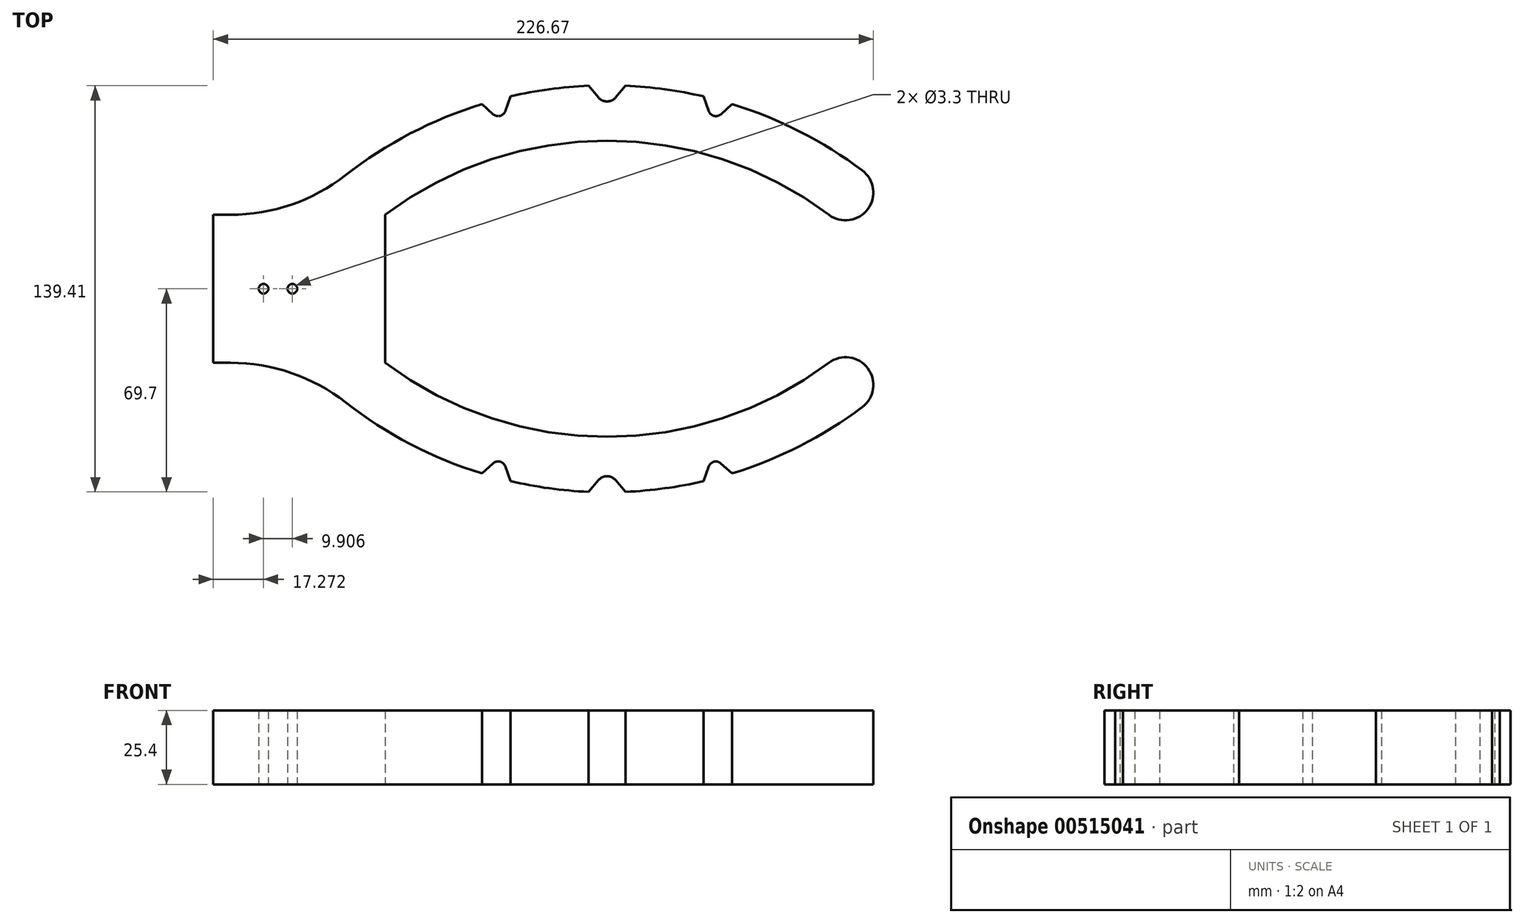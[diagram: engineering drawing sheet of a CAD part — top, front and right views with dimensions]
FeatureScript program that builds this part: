
annotation { "Feature Type Name" : "Feature", "Feature Type Description" : "" }
export const myFeature = defineFeature(function(context is Context, id is Id, definition is map)
    precondition{}
    {
        {
            var Q0;
            Q0=qCreatedBy(makeId("Top.planeOp"),FACE);
            var sketch = newSketch(context, id + "F0", { "sketchPlane" : qUnion([Q0])});
            skLineSegment(sketch, "E0.bottom", {"start": v(0, 0) * mm, "end": v(5.97, 0) * mm});
            skLineSegment(sketch, "E0.top", {"start": v(0, -50.8) * mm, "end": v(5.97, -50.8) * mm});
            skLineSegment(sketch, "E0.left", {"start": v(0, 0) * mm, "end": v(0, -50.8) * mm});
            skArc(sketch, "E1", {"start": v(211.43, 0) * mm, "mid": v(135.23, 25.4) * mm, "end": v(59.03, 0) * mm});
            skArc(sketch, "E2", {"start": v(59.06, -50.8) * mm, "mid": v(135.24, -76.19) * mm, "end": v(211.43, -50.8) * mm});
            skArc(sketch, "E3.0", {"start": v(222.86, 15.24) * mm, "mid": v(133.84, 44.44) * mm, "end": v(45.4, 13.56) * mm});
            skArc(sketch, "E4.0", {"start": v(45.45, -64.37) * mm, "mid": v(133.87, -95.23) * mm, "end": v(222.85, -66.04) * mm});
            skArc(sketch, "E5", {"start": v(211.43, 0) * mm, "mid": v(224.76, 1.9) * mm, "end": v(222.86, 15.24) * mm});
            skArc(sketch, "E6", {"start": v(222.85, -66.04) * mm, "mid": v(224.76, -52.7) * mm, "end": v(211.43, -50.8) * mm});
            skArc(sketch, "E7", {"start": v(5.97, 0) * mm, "mid": v(26.82, 3.48) * mm, "end": v(45.4, 13.56) * mm});
            skArc(sketch, "E8", {"start": v(45.45, -64.37) * mm, "mid": v(26.84, -54.29) * mm, "end": v(5.97, -50.8) * mm});
            skLineSegment(sketch, "E9", {"start": v(59.03, 0) * mm, "end": v(59.06, -50.8) * mm});
            skLineSegment(sketch, "E10", {"start": v(135.24, 50.81) * mm, "end": v(135.23, -101.6) * mm});
            skLineSegment(sketch, "E11", {"start": v(132.32, -91.04) * mm, "end": v(128.88, -95.1) * mm});
            skLineSegment(sketch, "E12", {"start": v(138.13, -91.04) * mm, "end": v(141.58, -95.1) * mm});
            skPoint(sketch, "E13.visualSharp", {"position": v(135.23, -87.62) * mm});
            skArc(sketch, "E13.filletArc", {"start": v(138.13, -91.04) * mm, "mid": v(135.23, -89.7) * mm, "end": v(132.32, -91.04) * mm});
            skLineSegment(sketch, "E14", {"start": v(135.23, -25.4) * mm, "end": v(230, -25.4) * mm});
            skLineSegment(sketch, "E15.MirrorCS", {"start": v(138.15, 40.25) * mm, "end": v(141.6, 44.31) * mm});
            skArc(sketch, "E16.MirrorCS", {"start": v(138.15, 40.25) * mm, "mid": v(135.24, 38.9) * mm, "end": v(132.34, 40.25) * mm});
            skLineSegment(sketch, "E17.MirrorCS", {"start": v(132.34, 40.25) * mm, "end": v(128.9, 44.31) * mm});
            skLineSegment(sketch, "E18", {"start": v(97.14, 50.81) * mm, "end": v(97.14, -102.44) * mm});
            skLineSegment(sketch, "E19", {"start": v(173.34, 50.81) * mm, "end": v(173.34, -98.72) * mm});
            skLineSegment(sketch, "E20", {"start": v(97.14, 39.4) * mm, "end": v(101.8, 20.92) * mm});
            skLineSegment(sketch, "E21", {"start": v(92.26, 37.99) * mm, "end": v(96.19, 34.5) * mm});
            skLineSegment(sketch, "E22", {"start": v(100.27, 35.56) * mm, "end": v(102.07, 40.64) * mm});
            skPoint(sketch, "E23.visualSharp", {"position": v(99, 32) * mm});
            skArc(sketch, "E23.filletArc", {"start": v(96.19, 34.5) * mm, "mid": v(98.5, 33.95) * mm, "end": v(100.27, 35.56) * mm});
            skLineSegment(sketch, "E24.MirrorCS", {"start": v(170.21, 35.55) * mm, "end": v(168.41, 40.63) * mm});
            skArc(sketch, "E25.MirrorCS", {"start": v(174.3, 34.5) * mm, "mid": v(171.97, 33.94) * mm, "end": v(170.21, 35.55) * mm});
            skLineSegment(sketch, "E26.MirrorCS", {"start": v(178.22, 37.98) * mm, "end": v(174.3, 34.5) * mm});
            skLineSegment(sketch, "E27.MirrorCS", {"start": v(178.2, -88.77) * mm, "end": v(174.28, -85.3) * mm});
            skArc(sketch, "E28.MirrorCS", {"start": v(174.28, -85.3) * mm, "mid": v(171.96, -84.74) * mm, "end": v(170.2, -86.35) * mm});
            skLineSegment(sketch, "E29.MirrorCS", {"start": v(170.2, -86.35) * mm, "end": v(168.4, -91.42) * mm});
            skLineSegment(sketch, "E30.MirrorCS", {"start": v(92.25, -88.76) * mm, "end": v(96.18, -85.29) * mm});
            skArc(sketch, "E31.MirrorCS", {"start": v(96.18, -85.29) * mm, "mid": v(98.5, -84.73) * mm, "end": v(100.25, -86.34) * mm});
            skLineSegment(sketch, "E32.MirrorCS", {"start": v(100.25, -86.34) * mm, "end": v(102.05, -91.42) * mm});
            skCircle(sketch, "E33", {"center": v(17.27, -25.4) * mm, "radius": 1.65 * mm});
            skCircle(sketch, "E34", {"center": v(27.18, -25.4) * mm, "radius": 1.65 * mm});
            skSolve(sketch);
        }
        {
            var Q0;
            {var subQ0=sQuery(id+"F0.wireOp",EDGE,"E7");Q0=makeQuery(id+"F0.imprint","IMPRINT",FACE,{"disambiguationData":[TD([[makeQuery(id+"F0.imprint","IMPRINT",EDGE,{"derivedFrom":subQ0}),-1.0]])]});}
            var Q1;
            {var subQ3=sQuery(id+"F0.wireOp",EDGE,"E0.left");Q1=makeQuery(id+"F0.imprint","IMPRINT",FACE,{"disambiguationData":[TD([[makeQuery(id+"F0.imprint","IMPRINT",EDGE,{"derivedFrom":subQ3}),1.0]])]});}
            var Q2;
            {var subQ0=sQuery(id+"F0.wireOp",EDGE,"E8");Q2=makeQuery(id+"F0.imprint","IMPRINT",FACE,{"disambiguationData":[TD([[makeQuery(id+"F0.imprint","IMPRINT",EDGE,{"derivedFrom":subQ0}),-1.0]])]});}
            var Q3;
            {var subQ5=sQuery(id+"F0.wireOp",EDGE,"E5");Q3=makeQuery(id+"F0.imprint","IMPRINT",FACE,{"disambiguationData":[TD([[makeQuery(id+"F0.imprint","IMPRINT",EDGE,{"derivedFrom":subQ5}),1.0]])]});}
            var Q4;
            {var subQ5=sQuery(id+"F0.wireOp",EDGE,"E6");Q4=makeQuery(id+"F0.imprint","IMPRINT",FACE,{"disambiguationData":[TD([[makeQuery(id+"F0.imprint","IMPRINT",EDGE,{"derivedFrom":subQ5}),1.0]])]});}
            var Q5;
            {var subQ7=sQuery(id+"F0.wireOp",EDGE,"E17.MirrorCS");Q5=makeQuery(id+"F0.imprint","IMPRINT",FACE,{"disambiguationData":[TD([[makeQuery(id+"F0.imprint","IMPRINT",EDGE,{"derivedFrom":subQ7}),1.0]])]});}
            var Q6;
            {var subQ0=sQuery(id+"F0.wireOp",EDGE,"E20");var subQ1=sQuery(id+"F0.wireOp",EDGE,"E1");var subQ2=makeQuery(id+"F0.imprint","INTERSECT",VERTEX,{"derivedFrom":[subQ1,subQ0]});Q6=makeQuery(id+"F0.imprint","IMPRINT",FACE,{"disambiguationData":[TD([[makeQuery(id+"F0.imprint","IMPRINT",EDGE,{"disambiguationData":[TD([[subQ2,-1.0]])],"derivedFrom":subQ1}),-1.0]])]});}
            var Q7;
            {var subQ0=sQuery(id+"F0.wireOp",EDGE,"E15.MirrorCS");Q7=makeQuery(id+"F0.imprint","IMPRINT",FACE,{"disambiguationData":[TD([[makeQuery(id+"F0.imprint","IMPRINT",EDGE,{"derivedFrom":subQ0}),-1.0]])]});}
            var Q8;
            {var subQ0=sQuery(id+"F0.wireOp",EDGE,"E12");Q8=makeQuery(id+"F0.imprint","IMPRINT",FACE,{"disambiguationData":[TD([[makeQuery(id+"F0.imprint","IMPRINT",EDGE,{"derivedFrom":subQ0}),1.0]])]});}
            var Q9;
            {var subQ0=sQuery(id+"F0.wireOp",EDGE,"E11");Q9=makeQuery(id+"F0.imprint","IMPRINT",FACE,{"disambiguationData":[TD([[makeQuery(id+"F0.imprint","IMPRINT",EDGE,{"derivedFrom":subQ0}),-1.0]])]});}
            extrude(context, id + "F1", {"entities" : qUnion([Q0, Q1, Q2, Q3, Q4, Q5, Q6, Q7, Q8, Q9]), "depth" : 25.4 * mm, "offsetDistance" : 25.4 * mm});
        }
    });
